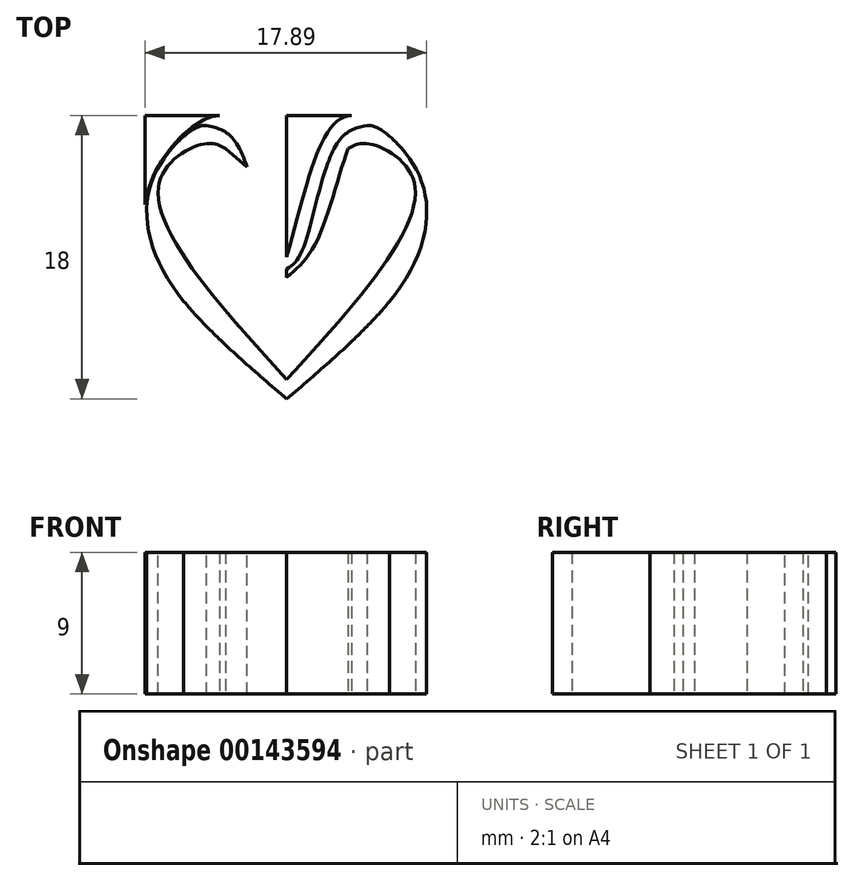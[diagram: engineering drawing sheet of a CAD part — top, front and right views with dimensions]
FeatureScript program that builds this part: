
annotation { "Feature Type Name" : "Feature", "Feature Type Description" : "" }
export const myFeature = defineFeature(function(context is Context, id is Id, definition is map)
    precondition{}
    {
        {
            var Q0;
            Q0=qCreatedBy(makeId("Top.planeOp"),FACE);
            var sketch = newSketch(context, id + "F0", { "sketchPlane" : qUnion([Q0])});
            skLineSegment(sketch, "E0.bottom", {"start": v(9, 9) * mm, "end": v(-9, 9) * mm});
            skLineSegment(sketch, "E0.top", {"start": v(9, -9) * mm, "end": v(-9, -9) * mm});
            skLineSegment(sketch, "E0.left", {"start": v(9, 9) * mm, "end": v(9, -9) * mm});
            skLineSegment(sketch, "E0.right", {"start": v(-9, 9) * mm, "end": v(-9, -9) * mm});
            skPoint(sketch, "E0.middle", {"position": v(0, 0) * mm});
            skFitSpline(sketch, "E1", {"points": [v(0, 0) * mm, v(-4.13, 9) * mm, v(-9, 3.33) * mm, v(0, -9) * mm], "startDerivative": vector(-12.78, 45.64) * mm, "endDerivative": vector(38.54, -32.76) * mm});
            skLineSegment(sketch, "E2", {"start": v(0, 9) * mm, "end": v(0, -9) * mm});
            skFitSpline(sketch, "E3.MirrorCS", {"points": [v(0, 0) * mm, v(4.13, 9) * mm, v(9, 3.33) * mm, v(0, -9) * mm], "startDerivative": vector(12.78, 45.64) * mm, "endDerivative": vector(-38.54, -32.76) * mm});
            skFitSpline(sketch, "E4", {"points": [v(0, -1.29) * mm, v(-1.84, 0.88) * mm, v(-3.9, 6.9) * mm, v(-5.1, 8.37) * mm, v(-7.02, 7.22) * mm, v(-8.8, 3.96) * mm, v(-7.7, -1.15) * mm, v(-2.7, -6.7) * mm, v(0, -9.03) * mm], "startDerivative": vector(-18.27, 15.46) * mm, "endDerivative": vector(20.35, -17.09) * mm});
            skFitSpline(sketch, "E5.MirrorCS", {"points": [v(0, -1.29) * mm, v(1.84, 0.88) * mm, v(3.9, 6.9) * mm, v(5.1, 8.37) * mm, v(7.02, 7.22) * mm, v(8.8, 3.96) * mm, v(7.7, -1.15) * mm, v(2.7, -6.7) * mm, v(0, -9.03) * mm], "startDerivative": vector(18.27, 15.46) * mm, "endDerivative": vector(-20.35, -17.09) * mm});
            skFitSpline(sketch, "E6", {"points": [v(-7.02, 7.22) * mm, v(-8.1, 4.72) * mm, v(-7.6, 0) * mm, v(-3.9, -5.61) * mm], "startDerivative": vector(-5.12, -8.75) * mm, "endDerivative": vector(10.92, -13.55) * mm});
            skFitSpline(sketch, "E7.MirrorCS", {"points": [v(7.02, 7.22) * mm, v(8.1, 4.72) * mm, v(7.6, 0) * mm, v(3.9, -5.61) * mm], "startDerivative": vector(5.12, -8.75) * mm, "endDerivative": vector(-10.92, -13.55) * mm});
            skFitSpline(sketch, "E8", {"points": [v(-3.9, 6.9) * mm, v(-5.1, 7.22) * mm, v(-8.1, 4.72) * mm, v(0, -7.77) * mm], "startDerivative": vector(-6.09, 3.65) * mm, "endDerivative": vector(23.72, -26.1) * mm});
            skFitSpline(sketch, "E9.MirrorCS", {"points": [v(3.9, 6.9) * mm, v(5.1, 7.22) * mm, v(8.1, 4.72) * mm, v(0, -7.77) * mm], "startDerivative": vector(6.09, 3.65) * mm, "endDerivative": vector(-23.72, -26.1) * mm});
            skFitSpline(sketch, "E10", {"points": [v(-5.1, 8.37) * mm, v(-3.54, 7.67) * mm, v(-1.95, 3.8) * mm, v(-0.77, 0) * mm, v(0, -0.74) * mm], "startDerivative": vector(8.08, -1.74) * mm, "endDerivative": vector(4.94, -3.29) * mm});
            skFitSpline(sketch, "E11", {"points": [v(-3.9, 6.9) * mm, v(-2.52, 5.74) * mm], "startDerivative": vector(1.37, -1.16) * mm, "endDerivative": vector(1.37, -1.16) * mm});
            skFitSpline(sketch, "E12.MirrorCS", {"points": [v(5.1, 8.37) * mm, v(3.54, 7.67) * mm, v(1.95, 3.8) * mm, v(0.77, 0) * mm, v(0, -0.74) * mm], "startDerivative": vector(-8.08, -1.74) * mm, "endDerivative": vector(-4.94, -3.29) * mm});
            skFitSpline(sketch, "E13.MirrorCS", {"points": [v(3.9, 6.9) * mm, v(2.52, 5.74) * mm], "startDerivative": vector(-1.37, -1.16) * mm, "endDerivative": vector(-1.37, -1.16) * mm});
            skSolve(sketch);
        }
        {
            var Q0;
            {var subQ0=sQuery(id+"F0.wireOp",EDGE,"E1");var subQ1=sQuery(id+"F0.wireOp",EDGE,"E0.bottom");var subQ9=makeQuery(id+"F0.imprint","INTERSECT",VERTEX,{"disambiguationData":[OD(0.0)],"derivedFrom":[subQ1,subQ0]});Q0=makeQuery(id+"F0.imprint","IMPRINT",FACE,{"disambiguationData":[TD([[makeQuery(id+"F0.imprint","IMPRINT",EDGE,{"disambiguationData":[TD([[subQ9,-1.0]])],"derivedFrom":subQ1}),1.0]])]});}
            var Q1;
            {var subQ0=sQuery(id+"F0.wireOp",EDGE,"E11");Q1=makeQuery(id+"F0.imprint","IMPRINT",FACE,{"disambiguationData":[TD([[makeQuery(id+"F0.imprint","IMPRINT",EDGE,{"derivedFrom":subQ0}),1.0]])]});}
            var Q2;
            {var subQ1=sQuery(id+"F0.wireOp",EDGE,"E4");var subQ3=sQuery(id+"F0.wireOp",EDGE,"E6");var subQ5=makeQuery(id+"F0.imprint","INTERSECT",VERTEX,{"disambiguationData":[OD(0.0)],"derivedFrom":[subQ1,subQ3]});Q2=makeQuery(id+"F0.imprint","IMPRINT",FACE,{"disambiguationData":[TD([[makeQuery(id+"F0.imprint","IMPRINT",EDGE,{"disambiguationData":[TD([[subQ5,1.0]])],"derivedFrom":subQ1}),1.0]])]});}
            var Q3;
            {var subQ1=sQuery(id+"F0.wireOp",EDGE,"E1");var subQ5=sQuery(id+"F0.wireOp",EDGE,"E4");var subQ7=makeQuery(id+"F0.imprint","INTERSECT",VERTEX,{"derivedFrom":[subQ1,subQ5]});Q3=makeQuery(id+"F0.imprint","IMPRINT",FACE,{"disambiguationData":[TD([[makeQuery(id+"F0.imprint","IMPRINT",EDGE,{"disambiguationData":[TD([[subQ7,-1.0]])],"derivedFrom":subQ1}),1.0]])]});}
            var Q4;
            {var subQ1=sQuery(id+"F0.wireOp",EDGE,"E1");var subQ3=sQuery(id+"F0.wireOp",EDGE,"E6");var subQ4=makeQuery(id+"F0.imprint","INTERSECT",VERTEX,{"derivedFrom":[subQ1,subQ3]});Q4=makeQuery(id+"F0.imprint","IMPRINT",FACE,{"disambiguationData":[TD([[makeQuery(id+"F0.imprint","IMPRINT",EDGE,{"disambiguationData":[TD([[subQ4,1.0]])],"derivedFrom":subQ3}),1.0]])]});}
            extrude(context, id + "F1", {"entities" : qUnion([Q0, Q1, Q2, Q3, Q4]), "depth" : 9 * mm});
        }
        {
            var Q0;
            {var subQ5=sQuery(id+"F0.wireOp",EDGE,"E3.MirrorCS");var subQ7=sQuery(id+"F0.wireOp",EDGE,"E0.bottom");var subQ8=makeQuery(id+"F0.imprint","INTERSECT",VERTEX,{"disambiguationData":[OD(0.0)],"derivedFrom":[subQ7,subQ5]});Q0=makeQuery(id+"F0.imprint","IMPRINT",FACE,{"disambiguationData":[TD([[makeQuery(id+"F0.imprint","IMPRINT",EDGE,{"disambiguationData":[TD([[subQ8,-1.0]])],"derivedFrom":subQ7}),1.0]])]});}
            var Q1;
            {var subQ5=sQuery(id+"F0.wireOp",EDGE,"E13.MirrorCS");Q1=makeQuery(id+"F0.imprint","IMPRINT",FACE,{"disambiguationData":[TD([[makeQuery(id+"F0.imprint","IMPRINT",EDGE,{"derivedFrom":subQ5}),1.0]])]});}
            var Q2;
            {var subQ1=sQuery(id+"F0.wireOp",EDGE,"E5.MirrorCS");var subQ5=sQuery(id+"F0.wireOp",EDGE,"E3.MirrorCS");var subQ6=makeQuery(id+"F0.imprint","INTERSECT",VERTEX,{"derivedFrom":[subQ5,subQ1]});Q2=makeQuery(id+"F0.imprint","IMPRINT",FACE,{"disambiguationData":[TD([[makeQuery(id+"F0.imprint","IMPRINT",EDGE,{"disambiguationData":[TD([[subQ6,-1.0]])],"derivedFrom":subQ5}),-1.0]])]});}
            var Q3;
            {var subQ0=sQuery(id+"F0.wireOp",EDGE,"E3.MirrorCS");var subQ5=sQuery(id+"F0.wireOp",EDGE,"E7.MirrorCS");var subQ6=makeQuery(id+"F0.imprint","INTERSECT",VERTEX,{"derivedFrom":[subQ0,subQ5]});Q3=makeQuery(id+"F0.imprint","IMPRINT",FACE,{"disambiguationData":[TD([[makeQuery(id+"F0.imprint","IMPRINT",EDGE,{"disambiguationData":[TD([[subQ6,1.0]])],"derivedFrom":subQ5}),-1.0]])]});}
            var Q4;
            {var subQ0=sQuery(id+"F0.wireOp",EDGE,"E13.MirrorCS");Q4=makeQuery(id+"F0.imprint","IMPRINT",FACE,{"disambiguationData":[TD([[makeQuery(id+"F0.imprint","IMPRINT",EDGE,{"derivedFrom":subQ0}),-1.0]])]});}
            var Q5;
            {var subQ1=sQuery(id+"F0.wireOp",EDGE,"E5.MirrorCS");var subQ3=sQuery(id+"F0.wireOp",EDGE,"E7.MirrorCS");var subQ5=makeQuery(id+"F0.imprint","INTERSECT",VERTEX,{"disambiguationData":[OD(0.0)],"derivedFrom":[subQ1,subQ3]});Q5=makeQuery(id+"F0.imprint","IMPRINT",FACE,{"disambiguationData":[TD([[makeQuery(id+"F0.imprint","IMPRINT",EDGE,{"disambiguationData":[TD([[subQ5,1.0]])],"derivedFrom":subQ1}),-1.0]])]});}
            extrude(context, id + "F2", {"entities" : qUnion([Q0, Q1, Q2, Q3, Q4, Q5]), "operationType" : NewBodyOperationType.ADD, "depth" : 9 * mm});
        }
    });
